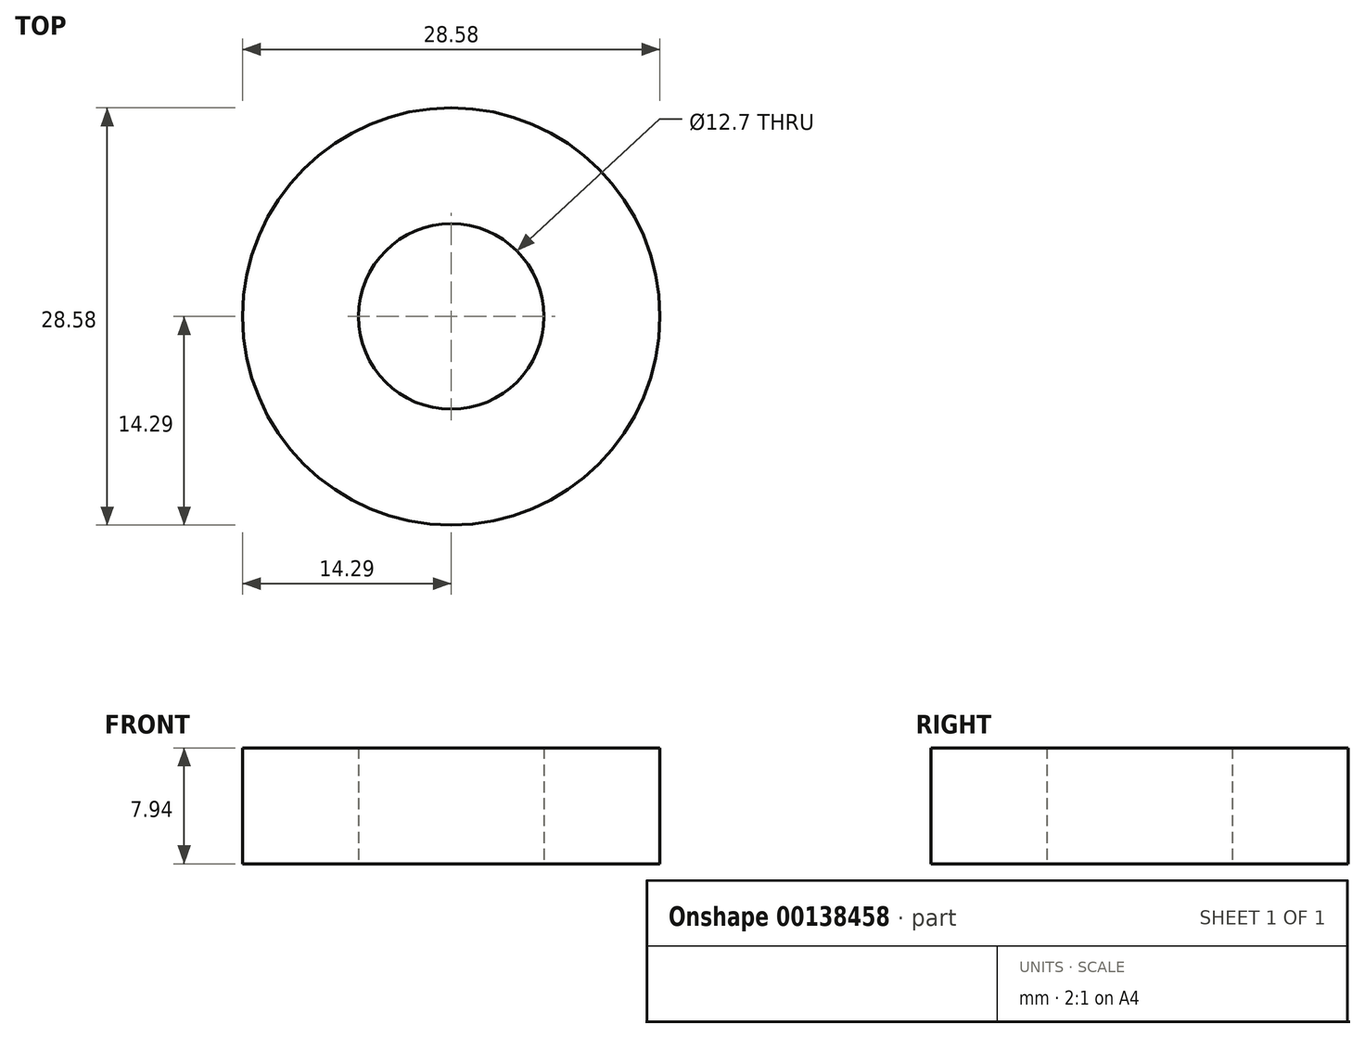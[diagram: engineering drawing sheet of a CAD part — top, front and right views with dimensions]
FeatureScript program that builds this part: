
annotation { "Feature Type Name" : "Feature", "Feature Type Description" : "" }
export const myFeature = defineFeature(function(context is Context, id is Id, definition is map)
    precondition{}
    {
        {
            var Q0;
            Q0=qCreatedBy(makeId("Top.planeOp"),FACE);
            var sketch = newSketch(context, id + "F0", { "sketchPlane" : qUnion([Q0])});
            skCircle(sketch, "E0", {"center": v(0, 0) * mm, "radius": 6.35 * mm});
            skCircle(sketch, "E1", {"center": v(0, 0) * mm, "radius": 14.29 * mm});
            skSolve(sketch);
        }
        {
            var Q0;
            Q0 = qSketchRegion(id + "F0", true);
            extrude(context, id + "F1", {"entities" : qUnion([Q0]), "depth" : 7.94 * mm});
        }
    });
